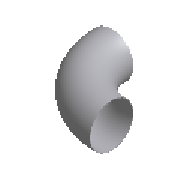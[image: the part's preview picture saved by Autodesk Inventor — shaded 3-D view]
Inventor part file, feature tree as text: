
AUTODESK INVENTOR PART (.ipt)
format: ipt  version: 2024.2 (Build 282272000, 272)  size: 183,296 bytes
history: native  units: mm (DEFAULTED — no unit token found)
features: other x4, sweep x1
ambient origin geometry x8: Origin, YZ Plane, XZ Plane, XY Plane, X Axis, Y Axis, Z Axis, Center Point
bodies: Solid1 (feature_tree)
feature tree (5):
  sweep  "Sweep1"
  other  "Work Point1"
  other  "Work Axis1"
  other  "Work Point2"
  other  "Work Axis2"
